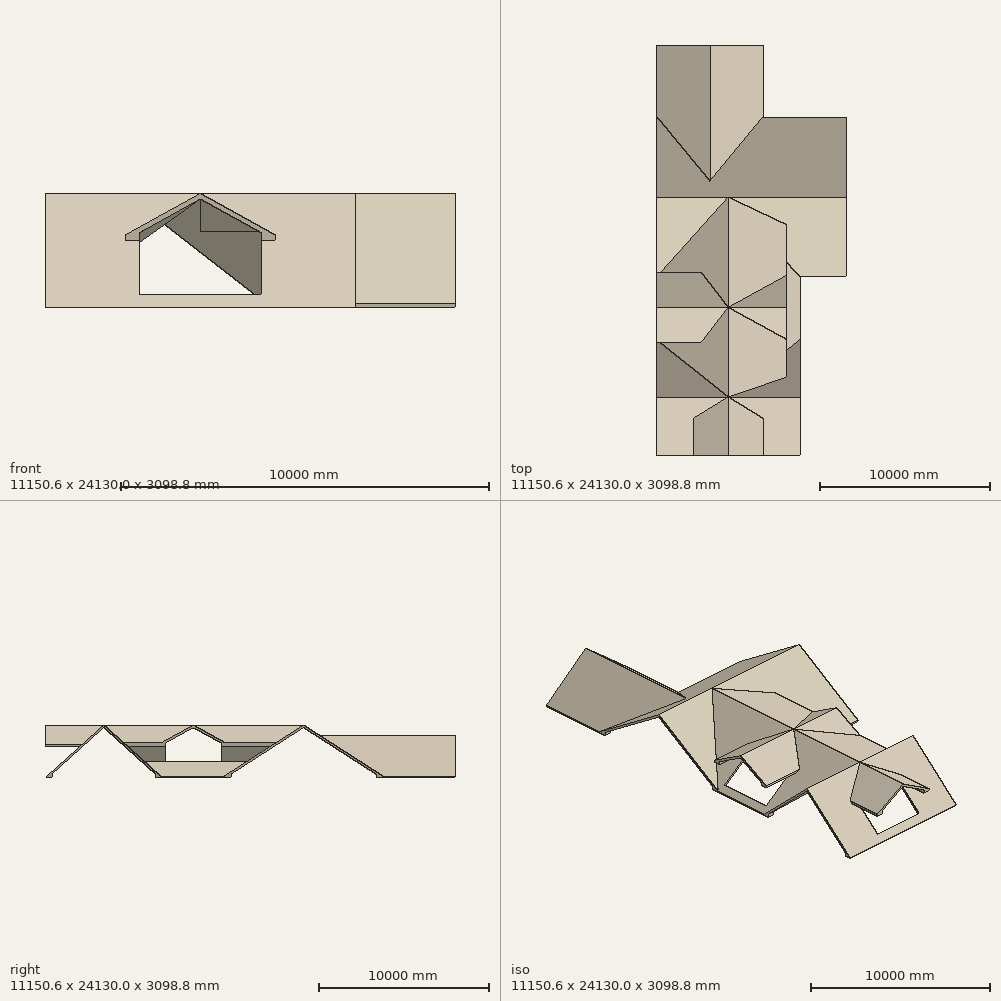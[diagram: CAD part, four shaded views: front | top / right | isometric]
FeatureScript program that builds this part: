
annotation { "Feature Type Name" : "Feature", "Feature Type Description" : "" }
export const myFeature = defineFeature(function(context is Context, id is Id, definition is map)
    precondition{}
    {
        {
            var Q0;
            Q0=qCreatedBy(makeId("Front.planeOp"),FACE);
            cPlane(context, id + "F0", {"entities" : qUnion([Q0]), "cplaneType" : CPlaneType.OFFSET, "offset" : 8928.1 * mm, "oppositeDirection" : true, "width" : 152.4 * mm, "height" : 152.4 * mm});
        }
        {
            var Q0;
            Q0=qCreatedBy(makeId("Front.planeOp"),FACE);
            cPlane(context, id + "F1", {"entities" : qUnion([Q0]), "cplaneType" : CPlaneType.OFFSET, "offset" : 6489.7 * mm, "width" : 152.4 * mm, "height" : 152.4 * mm});
        }
        {
            var Q0;
            Q0=qCreatedBy(makeId("Right.planeOp"),FACE);
            cPlane(context, id + "F2", {"entities" : qUnion([Q0]), "cplaneType" : CPlaneType.OFFSET, "offset" : 4216.4 * mm, "width" : 152.4 * mm, "height" : 152.4 * mm});
        }
        {
            var Q0;
            Q0=qCreatedBy(makeId("Front.planeOp"),FACE);
            cPlane(context, id + "F3", {"entities" : qUnion([Q0]), "cplaneType" : CPlaneType.OFFSET, "offset" : 11760.2 * mm, "width" : 152.4 * mm, "height" : 152.4 * mm});
        }
        {
            var Q0;
            Q0=qCreatedBy(makeId("Right.planeOp"),FACE);
            var sketch = newSketch(context, id + "F4", { "sketchPlane" : qUnion([Q0])});
            skLineSegment(sketch, "E0", {"start": v(-4267.2, 0) * mm, "end": v(4267.2, 0) * mm, "construction": true});
            skLineSegment(sketch, "E1", {"start": v(0, 0) * mm, "end": v(0, 2743.2) * mm, "construction": true});
            skLineSegment(sketch, "E2", {"start": v(0, 2743.2) * mm, "end": v(-4267.2, 0) * mm});
            skLineSegment(sketch, "E3", {"start": v(-4267.2, 0) * mm, "end": v(-4267.2, -203.2) * mm});
            skLineSegment(sketch, "E4", {"start": v(-4267.2, -203.2) * mm, "end": v(-4660.9, -203.2) * mm});
            skLineSegment(sketch, "E5", {"start": v(-4660.9, -203.2) * mm, "end": v(-4660.9, -100.7) * mm});
            skLineSegment(sketch, "E6", {"start": v(0, 2895.6) * mm, "end": v(-4660.9, -100.7) * mm});
            skLineSegment(sketch, "E7.MirrorCS", {"start": v(4267.2, 0) * mm, "end": v(4267.2, -203.2) * mm});
            skLineSegment(sketch, "E8.MirrorCS", {"start": v(4660.9, -203.2) * mm, "end": v(4660.9, -100.7) * mm});
            skLineSegment(sketch, "E9.MirrorCS", {"start": v(0, 2743.2) * mm, "end": v(4267.2, 0) * mm});
            skLineSegment(sketch, "E10.MirrorCS", {"start": v(4267.2, -203.2) * mm, "end": v(4660.9, -203.2) * mm});
            skLineSegment(sketch, "E11.MirrorCS", {"start": v(0, 2895.6) * mm, "end": v(4660.9, -100.7) * mm});
            skSolve(sketch);
        }
        {
            var Q0;
            Q0 = qSketchRegion(id + "F4", true);
            extrude(context, id + "F5", {"entities" : qUnion([Q0]), "depth" : 11150.6 * mm});
        }
        {
            var Q0;
            Q0=qCreatedBy(id+"F0.planeOp",FACE);
            var sketch = newSketch(context, id + "F6", { "sketchPlane" : qUnion([Q0])});
            skLineSegment(sketch, "E12", {"start": v(393.7, 0) * mm, "end": v(5880.1, 0) * mm, "construction": true});
            skLineSegment(sketch, "E13", {"start": v(5880.1, 0) * mm, "end": v(5880.1, -203.2) * mm});
            skLineSegment(sketch, "E14", {"start": v(3136.9, 0) * mm, "end": v(3136.9, 2133.6) * mm, "construction": true});
            skLineSegment(sketch, "E15", {"start": v(5880.1, -203.2) * mm, "end": v(393.7, -203.2) * mm});
            skLineSegment(sketch, "E16", {"start": v(5880.1, 0) * mm, "end": v(3136.9, 2133.6) * mm});
            skLineSegment(sketch, "E17.MirrorCS", {"start": v(393.7, 0) * mm, "end": v(3136.9, 2133.6) * mm});
            skLineSegment(sketch, "E18.MirrorCS", {"start": v(393.7, 0) * mm, "end": v(393.7, -203.2) * mm});
            skSolve(sketch);
        }
        {
            var Q0;
            Q0 = qSketchRegion(id + "F6", true);
            var Q1;
            Q1=qCreatedBy(makeId("Front.planeOp"),FACE);
            extrude(context, id + "F7", {"entities" : qUnion([Q0]), "operationType" : NewBodyOperationType.REMOVE, "endBound" : BoundingType.UP_TO_SURFACE, "endBoundEntityFace" : qUnion([Q1]), "depth" : 25.4 * mm});
        }
        {
            var Q0;
            Q0=qCreatedBy(id+"F0.planeOp",FACE);
            var sketch = newSketch(context, id + "F8", { "sketchPlane" : qUnion([Q0])});
            skLineSegment(sketch, "E19", {"start": v(393.7, 0) * mm, "end": v(5880.1, 0) * mm, "construction": true});
            skLineSegment(sketch, "E20", {"start": v(3136.9, 0) * mm, "end": v(3136.9, 2133.6) * mm, "construction": true});
            skLineSegment(sketch, "E21", {"start": v(5880.1, 0) * mm, "end": v(5880.1, -203.2) * mm});
            skLineSegment(sketch, "E22", {"start": v(5880.1, -203.2) * mm, "end": v(6273.8, -203.2) * mm});
            skLineSegment(sketch, "E23", {"start": v(6273.8, -203.2) * mm, "end": v(6273.8, -153.81) * mm});
            skLineSegment(sketch, "E24", {"start": v(5880.1, 0) * mm, "end": v(3136.9, 2133.6) * mm});
            skLineSegment(sketch, "E25", {"start": v(3136.9, 2286) * mm, "end": v(6273.8, -153.81) * mm});
            skLineSegment(sketch, "E26.MirrorCS", {"start": v(393.7, 0) * mm, "end": v(393.7, -203.2) * mm});
            skLineSegment(sketch, "E27.MirrorCS", {"start": v(0, -203.2) * mm, "end": v(0, -153.81) * mm});
            skLineSegment(sketch, "E28.MirrorCS", {"start": v(3136.9, 2286) * mm, "end": v(0, -153.81) * mm});
            skLineSegment(sketch, "E29.MirrorCS", {"start": v(393.7, -203.2) * mm, "end": v(0, -203.2) * mm});
            skLineSegment(sketch, "E30.MirrorCS", {"start": v(393.7, 0) * mm, "end": v(3136.9, 2133.6) * mm});
            skSolve(sketch);
        }
        {
            var Q0;
            Q0 = qSketchRegion(id + "F8", true);
            extrude(context, id + "F9", {"entities" : qUnion([Q0]), "operationType" : NewBodyOperationType.ADD, "endBound" : BoundingType.UP_TO_NEXT, "depth" : 25.4 * mm});
        }
        {
            var Q0;
            Q0=qCreatedBy(makeId("Right.planeOp"),FACE);
            var sketch = newSketch(context, id + "F10", { "sketchPlane" : qUnion([Q0])});
            skLineSegment(sketch, "E31", {"start": v(-14808.2, 0) * mm, "end": v(-8712.2, 0) * mm, "construction": true});
            skLineSegment(sketch, "E32", {"start": v(-11760.2, 0) * mm, "end": v(-11760.2, 2743.2) * mm, "construction": true});
            skLineSegment(sketch, "E33", {"start": v(-11760.2, 2743.2) * mm, "end": v(-14808.2, 0) * mm});
            skLineSegment(sketch, "E34", {"start": v(-14808.2, -203.2) * mm, "end": v(-15201.9, -203.2) * mm});
            skLineSegment(sketch, "E35", {"start": v(-15201.9, -203.2) * mm, "end": v(-15201.9, -201.93) * mm});
            skLineSegment(sketch, "E36", {"start": v(-14808.2, 0) * mm, "end": v(-14808.2, -203.2) * mm});
            skLineSegment(sketch, "E37", {"start": v(-11760.2, 2895.6) * mm, "end": v(-15201.9, -201.93) * mm});
            skLineSegment(sketch, "E38.MirrorCS", {"start": v(-8318.5, -203.2) * mm, "end": v(-8318.5, -201.93) * mm});
            skLineSegment(sketch, "E39.MirrorCS", {"start": v(-8712.2, 0) * mm, "end": v(-8712.2, -203.2) * mm});
            skLineSegment(sketch, "E40.MirrorCS", {"start": v(-8712.2, -203.2) * mm, "end": v(-8318.5, -203.2) * mm});
            skLineSegment(sketch, "E41.MirrorCS", {"start": v(-11760.2, 2895.6) * mm, "end": v(-8318.5, -201.93) * mm});
            skLineSegment(sketch, "E42.MirrorCS", {"start": v(-11760.2, 2743.2) * mm, "end": v(-8712.2, 0) * mm});
            skSolve(sketch);
        }
        {
            var Q0;
            Q0 = qSketchRegion(id + "F10", true);
            extrude(context, id + "F11", {"entities" : qUnion([Q0]), "operationType" : NewBodyOperationType.ADD, "depth" : 8432.8 * mm});
        }
        {
            var Q0;
            Q0=qCreatedBy(id+"F1.planeOp",FACE);
            var sketch = newSketch(context, id + "F12", { "sketchPlane" : qUnion([Q0])});
            skLineSegment(sketch, "E43", {"start": v(393.7, 0) * mm, "end": v(7226.3, 0) * mm, "construction": true});
            skLineSegment(sketch, "E44", {"start": v(4216.4, 0) * mm, "end": v(4216.4, 2743.2) * mm, "construction": true});
            skLineSegment(sketch, "E45", {"start": v(393.7, 0) * mm, "end": v(4216.4, 2743.2) * mm});
            skLineSegment(sketch, "E46", {"start": v(393.7, 0) * mm, "end": v(393.7, -203.2) * mm});
            skLineSegment(sketch, "E47", {"start": v(393.7, -203.2) * mm, "end": v(7226.3, -203.2) * mm});
            skLineSegment(sketch, "E48", {"start": v(7226.3, -203.2) * mm, "end": v(7226.3, 1828.8) * mm});
            skLineSegment(sketch, "E49", {"start": v(4216.4, 2743.2) * mm, "end": v(7226.3, 1828.8) * mm});
            skSolve(sketch);
        }
        {
            var Q0;
            Q0 = qSketchRegion(id + "F12", true);
            var Q1;
            Q1=qCreatedBy(makeId("Front.planeOp"),FACE);
            var Q2;
            Q2=qCreatedBy(id+"F3.planeOp",FACE);
            extrude(context, id + "F13", {"entities" : qUnion([Q0]), "operationType" : NewBodyOperationType.REMOVE, "endBound" : BoundingType.UP_TO_SURFACE, "oppositeDirection" : true, "endBoundEntityFace" : qUnion([Q1]), "depth" : 25.4 * mm, "hasSecondDirection" : true, "secondDirectionBound" : BoundingType.UP_TO_SURFACE, "secondDirectionOppositeDirection" : false, "secondDirectionBoundEntityFace" : qUnion([Q2]), "secondDirectionDepth" : 25.4 * mm});
        }
        {
            var Q0;
            Q0=qCreatedBy(id+"F1.planeOp",FACE);
            var sketch = newSketch(context, id + "F14", { "sketchPlane" : qUnion([Q0])});
            skLineSegment(sketch, "E50", {"start": v(393.7, 0) * mm, "end": v(8039.1, 0) * mm, "construction": true});
            skLineSegment(sketch, "E51", {"start": v(7226.3, 0) * mm, "end": v(7226.3, 1828.8) * mm, "construction": true});
            skLineSegment(sketch, "E52", {"start": v(4216.4, 0) * mm, "end": v(4216.4, 2743.2) * mm, "construction": true});
            skLineSegment(sketch, "E53", {"start": v(4216.4, 2743.2) * mm, "end": v(4216.4, 2895.6) * mm});
            skLineSegment(sketch, "E54", {"start": v(393.7, 0) * mm, "end": v(4216.4, 2743.2) * mm});
            skLineSegment(sketch, "E55", {"start": v(4216.4, 2895.6) * mm, "end": v(0, -130.12) * mm});
            skLineSegment(sketch, "E56", {"start": v(393.7, 0) * mm, "end": v(393.7, -203.2) * mm});
            skLineSegment(sketch, "E57", {"start": v(393.7, -203.2) * mm, "end": v(0, -203.2) * mm});
            skLineSegment(sketch, "E58", {"start": v(0, -203.2) * mm, "end": v(0, -130.12) * mm});
            skLineSegment(sketch, "E59.MirrorCS", {"start": v(8432.8, -203.2) * mm, "end": v(8432.8, -130.12) * mm});
            skLineSegment(sketch, "E60", {"start": v(8432.8, -203.2) * mm, "end": v(7226.3, -203.2) * mm});
            skLineSegment(sketch, "E61", {"start": v(7226.3, -203.2) * mm, "end": v(7226.3, 735.67) * mm});
            skLineSegment(sketch, "E62", {"start": v(7226.3, 735.67) * mm, "end": v(8432.8, -130.12) * mm});
            skLineSegment(sketch, "E63", {"start": v(4216.4, 2743.2) * mm, "end": v(7226.3, 1828.8) * mm});
            skLineSegment(sketch, "E64", {"start": v(7226.3, 1828.8) * mm, "end": v(7226.3, 1625.6) * mm});
            skLineSegment(sketch, "E65", {"start": v(7226.3, 1625.6) * mm, "end": v(7620, 1625.6) * mm});
            skLineSegment(sketch, "E66", {"start": v(7620, 1625.6) * mm, "end": v(7620, 1861.6) * mm});
            skLineSegment(sketch, "E67", {"start": v(4216.4, 2895.6) * mm, "end": v(7620, 1861.6) * mm});
            skSolve(sketch);
        }
        {
            var Q0;
            Q0 = qSketchRegion(id + "F14", true);
            extrude(context, id + "F15", {"entities" : qUnion([Q0]), "operationType" : NewBodyOperationType.ADD, "endBound" : BoundingType.UP_TO_NEXT, "oppositeDirection" : true, "depth" : 25.4 * mm, "hasSecondDirection" : true, "secondDirectionBound" : BoundingType.UP_TO_NEXT, "secondDirectionOppositeDirection" : false, "secondDirectionDepth" : 25.4 * mm});
        }
        {
            var Q0;
            Q0=makeQuery(id+"F15.opExtrude","SWEPT_FACE",FACE,{"disambiguationData":[OSD([sQuery(id+"F14.wireOp",EDGE,"E66")])]});
            var sketch = newSketch(context, id + "F16", { "sketchPlane" : qUnion([Q0])});
            skLineSegment(sketch, "E68", {"start": v(0, 0) * mm, "end": v(-6489.7, 0) * mm, "construction": true});
            skLineSegment(sketch, "E69", {"start": v(-6489.7, 0) * mm, "end": v(-6489.7, 2743.2) * mm, "construction": true});
            skLineSegment(sketch, "E70", {"start": v(-6489.7, 0) * mm, "end": v(-8140.7, 0) * mm, "construction": true});
            skLineSegment(sketch, "E71", {"start": v(-8140.7, 0) * mm, "end": v(-8140.7, 1828.8) * mm, "construction": true});
            skLineSegment(sketch, "E72", {"start": v(-6489.7, 2743.2) * mm, "end": v(-8140.7, 1828.8) * mm});
            skLineSegment(sketch, "E73", {"start": v(-8140.7, 1828.8) * mm, "end": v(-8140.7, 1625.6) * mm});
            skLineSegment(sketch, "E74", {"start": v(-8140.7, 1625.6) * mm, "end": v(-4838.7, 1625.6) * mm});
            skLineSegment(sketch, "E75.MirrorCS", {"start": v(-4838.7, 1828.8) * mm, "end": v(-4838.7, 1625.6) * mm});
            skLineSegment(sketch, "E76.MirrorCS", {"start": v(-6489.7, 2743.2) * mm, "end": v(-4838.7, 1828.8) * mm});
            skSolve(sketch);
        }
        {
            var Q0;
            Q0 = qSketchRegion(id + "F16", true);
            var Q1;
            Q1=qCreatedBy(id+"F2.planeOp",FACE);
            extrude(context, id + "F17", {"entities" : qUnion([Q0]), "operationType" : NewBodyOperationType.REMOVE, "endBound" : BoundingType.UP_TO_SURFACE, "oppositeDirection" : true, "endBoundEntityFace" : qUnion([Q1]), "depth" : 25.4 * mm});
        }
        {
            var Q0;
            Q0=makeQuery(id+"F17.boolean.opBoolean","SPLIT",FACE,{"disambiguationData":[TD([makeQuery(id+"F5.opExtrude","SWEPT_FACE",FACE,{"disambiguationData":[OSD([sQuery(id+"F4.wireOp",EDGE,"E6")])]})])],"derivedFrom":makeQuery(id+"F15.opExtrude","SWEPT_FACE",FACE,{"disambiguationData":[OSD([sQuery(id+"F14.wireOp",EDGE,"E66")])]})});
            var sketch = newSketch(context, id + "F18", { "sketchPlane" : qUnion([Q0])});
            skLineSegment(sketch, "E77", {"start": v(0, 0) * mm, "end": v(-6489.7, 0) * mm, "construction": true});
            skLineSegment(sketch, "E78", {"start": v(-6489.7, 0) * mm, "end": v(-6489.7, 2743.2) * mm, "construction": true});
            skLineSegment(sketch, "E79", {"start": v(-6489.7, 0) * mm, "end": v(-8140.7, 0) * mm, "construction": true});
            skLineSegment(sketch, "E80", {"start": v(-8140.7, 0) * mm, "end": v(-8140.7, 1828.8) * mm, "construction": true});
            skLineSegment(sketch, "E81", {"start": v(-6489.7, 2743.2) * mm, "end": v(-8081.49, 1861.6) * mm});
            skLineSegment(sketch, "E82", {"start": v(-6489.7, 2895.6) * mm, "end": v(-8356.65, 1861.6) * mm});
            skLineSegment(sketch, "E83", {"start": v(-8356.65, 1861.6) * mm, "end": v(-8081.49, 1861.6) * mm});
            skLineSegment(sketch, "E84.MirrorCS", {"start": v(-4622.75, 1861.6) * mm, "end": v(-4897.91, 1861.6) * mm});
            skLineSegment(sketch, "E85.MirrorCS", {"start": v(-6489.7, 2895.6) * mm, "end": v(-4622.75, 1861.6) * mm});
            skLineSegment(sketch, "E86.MirrorCS", {"start": v(-6489.7, 2743.2) * mm, "end": v(-4897.91, 1861.6) * mm});
            skSolve(sketch);
        }
        {
            var Q0;
            Q0 = qSketchRegion(id + "F18", true);
            var Q1;
            Q1=makeQuery(id+"F15.opExtrude","SWEPT_FACE",FACE,{"disambiguationData":[OSD([sQuery(id+"F14.wireOp",EDGE,"E67")])]});
            var Q2;
            Q2=qCreatedBy(id+"F2.planeOp",FACE);
            extrude(context, id + "F19", {"entities" : qUnion([Q0, Q1]), "operationType" : NewBodyOperationType.ADD, "endBound" : BoundingType.UP_TO_SURFACE, "oppositeDirection" : true, "endBoundEntityFace" : qUnion([Q2]), "depth" : 25.4 * mm});
        }
        {
            var Q0;
            {var subQ0=makeQuery(id+"F13.opExtrude","SWEPT_FACE",FACE,{"disambiguationData":[OSD([sQuery(id+"F12.wireOp",EDGE,"E46")])]});Q0=makeQuery(id+"F15.boolean.opBoolean","MERGE",FACE,{"derivedFrom":[makeQuery(id+"F13.boolean.opBoolean","COPY",FACE,{"disambiguationData":[OD(0.0)],"derivedFrom":subQ0}),makeQuery(id+"F13.boolean.opBoolean","COPY",FACE,{"disambiguationData":[OD(1.0)],"derivedFrom":subQ0}),makeQuery(id+"F15.opExtrude","SWEPT_FACE",FACE,{"disambiguationData":[OSD([sQuery(id+"F14.wireOp",EDGE,"E56")])]})]});}
            var sketch = newSketch(context, id + "F20", { "sketchPlane" : qUnion([Q0])});
            skLineSegment(sketch, "E87", {"start": v(0, 0) * mm, "end": v(-6489.7, 0) * mm, "construction": true});
            skLineSegment(sketch, "E88", {"start": v(-6489.7, 0) * mm, "end": v(-6489.7, 2743.2) * mm, "construction": true});
            skLineSegment(sketch, "E89", {"start": v(-8140.7, 0) * mm, "end": v(-4838.7, 0) * mm});
            skLineSegment(sketch, "E90", {"start": v(-8140.7, 0) * mm, "end": v(-8140.7, 1828.8) * mm});
            skLineSegment(sketch, "E91", {"start": v(-8140.7, 1828.8) * mm, "end": v(-6489.7, 2743.2) * mm});
            skLineSegment(sketch, "E92.MirrorCS", {"start": v(-4838.7, 0) * mm, "end": v(-4838.7, 1828.8) * mm});
            skLineSegment(sketch, "E93.MirrorCS", {"start": v(-4838.7, 1828.8) * mm, "end": v(-6489.7, 2743.2) * mm});
            skSolve(sketch);
        }
        {
            var Q0;
            Q0 = qSketchRegion(id + "F20", true);
            var Q1;
            Q1=qCreatedBy(id+"F2.planeOp",FACE);
            extrude(context, id + "F21", {"entities" : qUnion([Q0]), "operationType" : NewBodyOperationType.REMOVE, "endBound" : BoundingType.UP_TO_SURFACE, "endBoundEntityFace" : qUnion([Q1]), "depth" : 25.4 * mm});
        }
        {
            var Q0;
            Q0=qCreatedBy(makeId("Right.planeOp"),FACE);
            var sketch = newSketch(context, id + "F22", { "sketchPlane" : qUnion([Q0])});
            skLineSegment(sketch, "E94", {"start": v(0, 0) * mm, "end": v(-6489.7, 0) * mm, "construction": true});
            skLineSegment(sketch, "E95", {"start": v(-8140.7, 0) * mm, "end": v(-6489.7, 0) * mm, "construction": true});
            skLineSegment(sketch, "E96", {"start": v(-6489.7, 0) * mm, "end": v(-6489.7, 2743.2) * mm, "construction": true});
            skLineSegment(sketch, "E97", {"start": v(-8140.7, 0) * mm, "end": v(-8140.7, 1828.8) * mm, "construction": true});
            skLineSegment(sketch, "E98", {"start": v(-6489.7, 2743.2) * mm, "end": v(-8140.7, 1828.8) * mm});
            skLineSegment(sketch, "E99", {"start": v(-8140.7, 1625.6) * mm, "end": v(-8534.4, 1625.6) * mm});
            skLineSegment(sketch, "E100", {"start": v(-8534.4, 1625.6) * mm, "end": v(-8534.4, 1763.15) * mm});
            skLineSegment(sketch, "E101", {"start": v(-8140.7, 1828.8) * mm, "end": v(-8140.7, 1625.6) * mm});
            skLineSegment(sketch, "E102", {"start": v(-6489.7, 2895.6) * mm, "end": v(-8534.4, 1763.15) * mm});
            skLineSegment(sketch, "E103.MirrorCS", {"start": v(-4838.7, 1828.8) * mm, "end": v(-4838.7, 1625.6) * mm});
            skLineSegment(sketch, "E104.MirrorCS", {"start": v(-4445, 1625.6) * mm, "end": v(-4445, 1763.15) * mm});
            skLineSegment(sketch, "E105.MirrorCS", {"start": v(-6489.7, 2895.6) * mm, "end": v(-4445, 1763.15) * mm});
            skLineSegment(sketch, "E106.MirrorCS", {"start": v(-4838.7, 1625.6) * mm, "end": v(-4445, 1625.6) * mm});
            skLineSegment(sketch, "E107.MirrorCS", {"start": v(-6489.7, 2743.2) * mm, "end": v(-4838.7, 1828.8) * mm});
            skSolve(sketch);
        }
        {
            var Q0;
            Q0 = qSketchRegion(id + "F22", true);
            extrude(context, id + "F23", {"entities" : qUnion([Q0]), "operationType" : NewBodyOperationType.ADD, "endBound" : BoundingType.UP_TO_NEXT, "depth" : 25.4 * mm});
        }
        {
            var Q0;
            Q0=makeQuery(id+"F11.opExtrude","SWEPT_FACE",FACE,{"disambiguationData":[OSD([sQuery(id+"F10.wireOp",EDGE,"E36")])]});
            var sketch = newSketch(context, id + "F24", { "sketchPlane" : qUnion([Q0])});
            skLineSegment(sketch, "E108", {"start": v(-2565.4, 0) * mm, "end": v(-5867.4, 0) * mm});
            skLineSegment(sketch, "E109", {"start": v(-4216.4, 0) * mm, "end": v(-4216.4, 2743.2) * mm, "construction": true});
            skLineSegment(sketch, "E110", {"start": v(-2565.4, 0) * mm, "end": v(-2565.4, 1828.8) * mm});
            skLineSegment(sketch, "E111", {"start": v(-2565.4, 1828.8) * mm, "end": v(-4216.4, 2743.2) * mm});
            skLineSegment(sketch, "E112.MirrorCS", {"start": v(-5867.4, 1828.8) * mm, "end": v(-4216.4, 2743.2) * mm});
            skLineSegment(sketch, "E113.MirrorCS", {"start": v(-5867.4, 0) * mm, "end": v(-5867.4, 1828.8) * mm});
            skSolve(sketch);
        }
        {
            var Q0;
            Q0 = qSketchRegion(id + "F24", true);
            var Q1;
            Q1=qCreatedBy(id+"F3.planeOp",FACE);
            extrude(context, id + "F25", {"entities" : qUnion([Q0]), "operationType" : NewBodyOperationType.REMOVE, "endBound" : BoundingType.UP_TO_SURFACE, "endBoundEntityFace" : qUnion([Q1]), "depth" : 25.4 * mm});
        }
        {
            var Q0;
            Q0=makeQuery(id+"F11.opExtrude","SWEPT_FACE",FACE,{"disambiguationData":[OSD([sQuery(id+"F10.wireOp",EDGE,"E35")])]});
            var sketch = newSketch(context, id + "F26", { "sketchPlane" : qUnion([Q0])});
            skLineSegment(sketch, "E114", {"start": v(2565.4, 0) * mm, "end": v(5867.4, 0) * mm, "construction": true});
            skLineSegment(sketch, "E115", {"start": v(4216.4, 0) * mm, "end": v(4216.4, 2743.2) * mm, "construction": true});
            skLineSegment(sketch, "E116", {"start": v(2565.4, 0) * mm, "end": v(2565.4, 1828.8) * mm, "construction": true});
            skLineSegment(sketch, "E117", {"start": v(4216.4, 2743.2) * mm, "end": v(2565.4, 1828.8) * mm});
            skLineSegment(sketch, "E118", {"start": v(2565.4, 1828.8) * mm, "end": v(2565.4, 1625.6) * mm});
            skLineSegment(sketch, "E119", {"start": v(2565.4, 1625.6) * mm, "end": v(2171.7, 1625.6) * mm});
            skLineSegment(sketch, "E120", {"start": v(2171.7, 1625.6) * mm, "end": v(2171.7, 1763.15) * mm});
            skLineSegment(sketch, "E121", {"start": v(4216.4, 2895.6) * mm, "end": v(2171.7, 1763.15) * mm});
            skLineSegment(sketch, "E122.MirrorCS", {"start": v(6261.1, 1625.6) * mm, "end": v(6261.1, 1763.15) * mm});
            skLineSegment(sketch, "E123.MirrorCS", {"start": v(4216.4, 2743.2) * mm, "end": v(5867.4, 1828.8) * mm});
            skLineSegment(sketch, "E124.MirrorCS", {"start": v(5867.4, 1828.8) * mm, "end": v(5867.4, 1625.6) * mm});
            skLineSegment(sketch, "E125.MirrorCS", {"start": v(5867.4, 1625.6) * mm, "end": v(6261.1, 1625.6) * mm});
            skLineSegment(sketch, "E126.MirrorCS", {"start": v(4216.4, 2895.6) * mm, "end": v(6261.1, 1763.15) * mm});
            skSolve(sketch);
        }
        {
            var Q0;
            Q0 = qSketchRegion(id + "F26", true);
            extrude(context, id + "F27", {"entities" : qUnion([Q0]), "operationType" : NewBodyOperationType.ADD, "endBound" : BoundingType.UP_TO_NEXT, "oppositeDirection" : true, "depth" : 25.4 * mm});
        }
    });
